# Revit family: LOROWERK 01385-000X
name_source: partatom
category: Sanitärinstallationen
revit_build: Autodesk Revit 2017 (Build: 20160225_1515(x64)
units: mm (PartAtom-declared; Revit-internal decimal feet)

## family parameters
Arbeitsebenenbasiert = Nein
Beim Laden mit Abzugskörper schneiden = Nein
Bemaßung runder Anschluss = Durchmesser verwenden
Gemeinsam genutzt = Nein
Immer vertikal = Ja
Raumberechnungspunkt = Nein
Teiletyp = Normal

## types (1)
- LOROWERK 01385-000X
    Anschluss an GLT, GA = Nein
    Beschreibung = LORO-Wärmedämmblock für Attika-Haupt-Not-Kombi
    Brandschutz mit Klasse R 120 nachrüstbar = Nein
    DATANORM = 01385.000X
    Elektrischer Anschluss YesNo = Nein
    GTIN = 4038088086278
    HAN = 01385.000X
    HeinzeBIM = https://www.heinze.de
    Hersteller = LOROWERK K.H. Vahlbrauk GmbH & Co. KG
    Komplettartikel (Einteilig) aus Kombination (Mehrteileausführung) Ablaufgrundkörper und Aufsatzstück = Nein
    Potenzialausgleich (Erdungsanschluss) vorhanden = Nein
    Produktfamilie = LORO-Wärmedämmblock für Attika-Haupt-Not-Kombi
    Produktklassifikation Text = Zubehoer
    Produktname = LORO-Wärmedämmblock für Attika-Haupt-Not-Kombi
    Typname = LORO-Wärmedämmblock für Attika-Haupt-Not-Kombi
    VDIBSN = 100003000???0000000000000000000000000000000000000100000000
